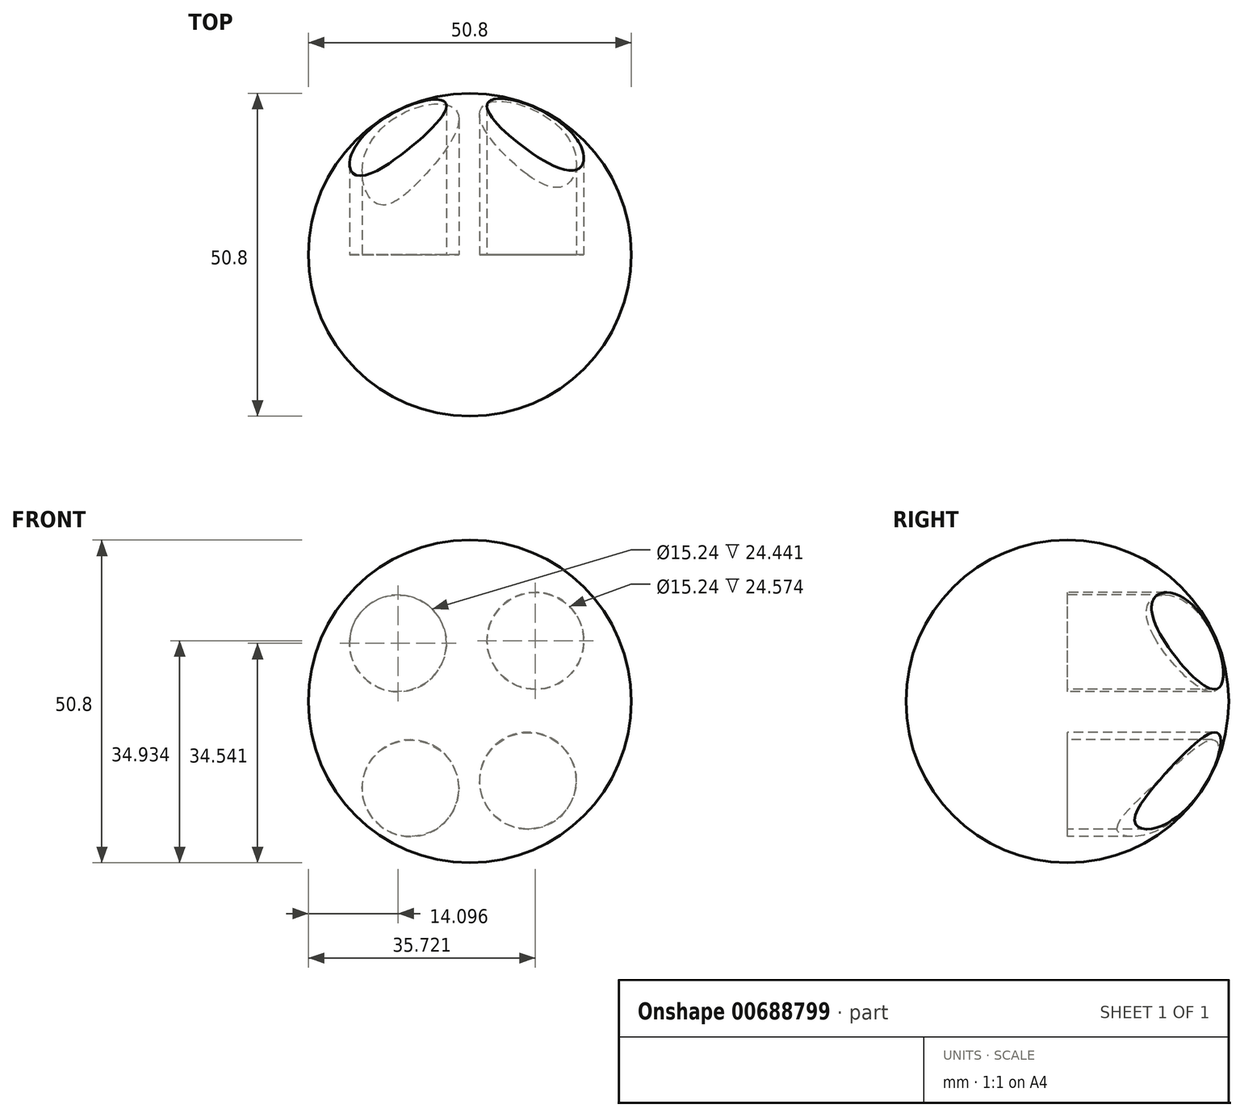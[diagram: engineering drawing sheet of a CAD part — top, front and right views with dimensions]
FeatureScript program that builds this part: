
annotation { "Feature Type Name" : "Feature", "Feature Type Description" : "" }
export const myFeature = defineFeature(function(context is Context, id is Id, definition is map)
    precondition{}
    {
        {
            var Q0;
            Q0=qCreatedBy(makeId("Front.planeOp"),FACE);
            var sketch = newSketch(context, id + "F0", { "sketchPlane" : qUnion([Q0])});
            skArc(sketch, "E0", {"start": v(0, 25.4) * mm, "mid": v(-25.4, 0) * mm, "end": v(0, -25.4) * mm});
            skLineSegment(sketch, "E1", {"start": v(0, 25.4) * mm, "end": v(0, -25.4) * mm});
            skSolve(sketch);
        }
        {
            var Q0;
            Q0=makeQuery(id+"F0.imprint","IMPRINT",FACE,{"disambiguationData":[TD([[makeQuery(id+"F0.imprint","IMPRINT",EDGE,{"derivedFrom":sQuery(id+"F0.wireOp",EDGE,"E0")}),1.0]])]});
            var Q1;
            Q1=sQuery(id+"F0.wireOp",EDGE,"E1");
            revolve(context, id + "F1", {"entities" : qUnion([Q0]), "axis" : qUnion([Q1]), "revolveType" : RevolveType.FULL});
        }
        {
            var Q0;
            Q0=qCreatedBy(makeId("Front.planeOp"),FACE);
            var sketch = newSketch(context, id + "F2", { "sketchPlane" : qUnion([Q0])});
            skCircle(sketch, "E2", {"center": v(10.32, 9.53) * mm, "radius": 7.62 * mm});
            skCircle(sketch, "E3", {"center": v(-11.3, 9.14) * mm, "radius": 7.62 * mm});
            skCircle(sketch, "E4", {"center": v(9.14, -12.48) * mm, "radius": 7.62 * mm});
            skCircle(sketch, "E5", {"center": v(-9.34, -13.66) * mm, "radius": 7.62 * mm});
            skSolve(sketch);
        }
        {
            var Q0;
            Q0=makeQuery(id+"F2.imprint","IMPRINT",FACE,{"disambiguationData":[TD([[makeQuery(id+"F2.imprint","IMPRINT",EDGE,{"derivedFrom":sQuery(id+"F2.wireOp",EDGE,"E3")}),1.0]])]});
            var Q1;
            Q1=makeQuery(id+"F2.imprint","IMPRINT",FACE,{"disambiguationData":[TD([[makeQuery(id+"F2.imprint","IMPRINT",EDGE,{"derivedFrom":sQuery(id+"F2.wireOp",EDGE,"E2")}),1.0]])]});
            var Q2;
            Q2=makeQuery(id+"F2.imprint","IMPRINT",FACE,{"disambiguationData":[TD([[makeQuery(id+"F2.imprint","IMPRINT",EDGE,{"derivedFrom":sQuery(id+"F2.wireOp",EDGE,"E4")}),1.0]])]});
            var Q3;
            Q3=makeQuery(id+"F2.imprint","IMPRINT",FACE,{"disambiguationData":[TD([[makeQuery(id+"F2.imprint","IMPRINT",EDGE,{"derivedFrom":sQuery(id+"F2.wireOp",EDGE,"E5")}),1.0]])]});
            extrude(context, id + "F3", {"entities" : qUnion([Q0, Q1, Q2, Q3]), "operationType" : NewBodyOperationType.REMOVE, "oppositeDirection" : true, "depth" : 76.2 * mm, "offsetDistance" : 25.4 * mm});
        }
    });
